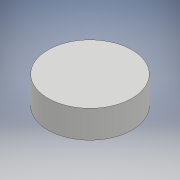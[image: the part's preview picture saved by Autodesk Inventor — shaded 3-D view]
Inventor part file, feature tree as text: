
AUTODESK INVENTOR PART (.ipt)
format: ipt  version: 2017 SP1 (Build 210196100, 196)  size: 87,040 bytes
history: native  units: mm
features: extrude x1, sketch x1
ambient origin geometry x8: Origin, YZ Plane, XZ Plane, XY Plane, X Axis, Y Axis, Z Axis, Center Point
bodies: Solide1 (feature_tree)
feature tree (2):
  extrude  "Extrusion1"  Depth=10.0mm TaperAngle=0.0deg
  sketch  "Esquisse1"
